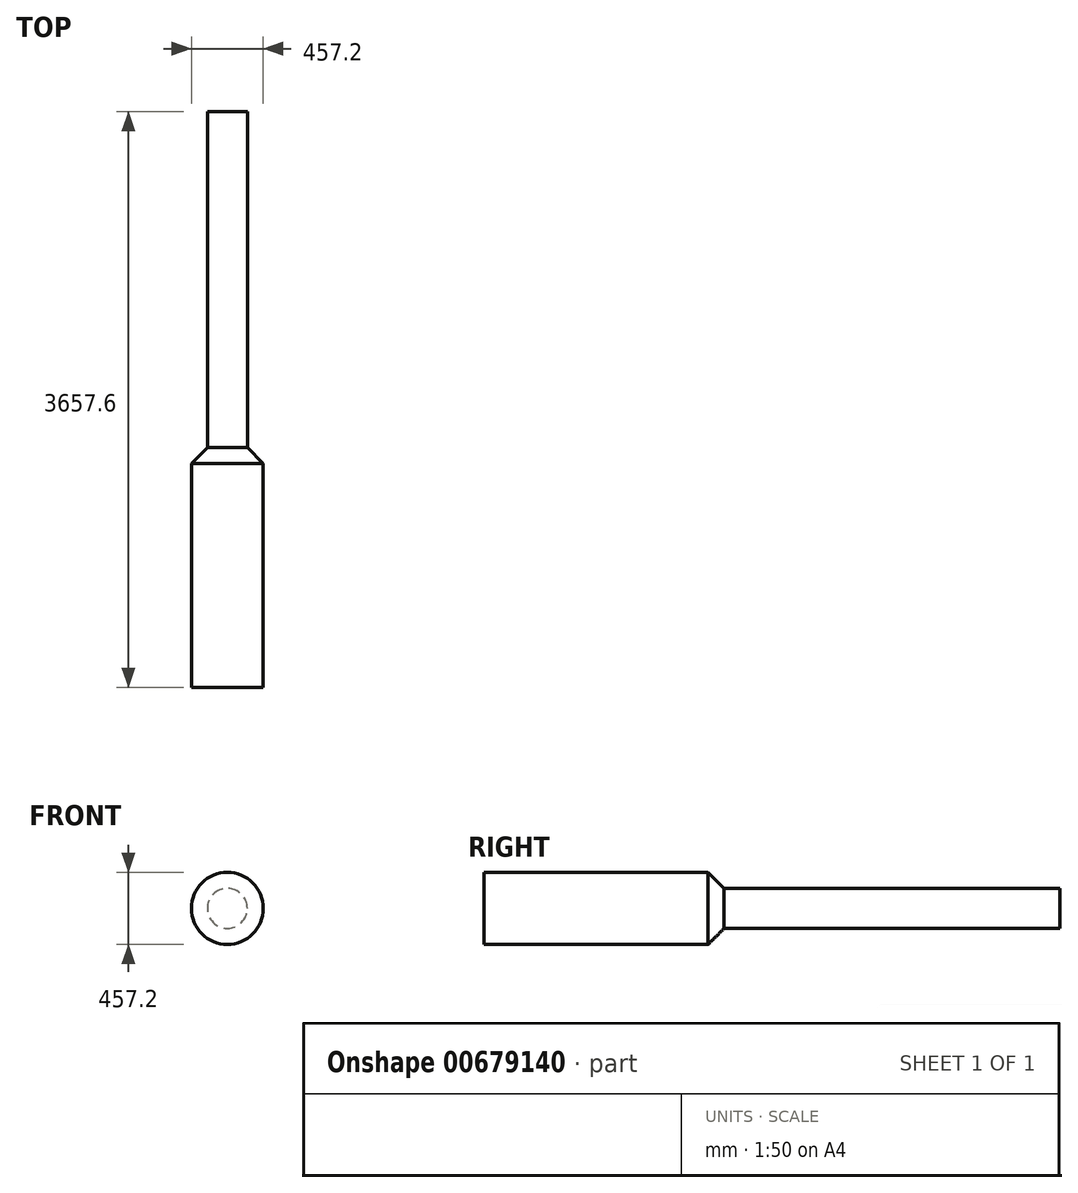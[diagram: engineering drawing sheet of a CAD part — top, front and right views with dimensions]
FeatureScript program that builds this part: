
annotation { "Feature Type Name" : "Feature", "Feature Type Description" : "" }
export const myFeature = defineFeature(function(context is Context, id is Id, definition is map)
    precondition{}
    {
        {
            var Q0;
            Q0=qCreatedBy(makeId("Right.planeOp"),FACE);
            var sketch = newSketch(context, id + "F0", { "sketchPlane" : qUnion([Q0])});
            skLineSegment(sketch, "E0.top", {"start": v(0, 228.6) * mm, "end": v(1422.4, 228.6) * mm});
            skLineSegment(sketch, "E0.left", {"start": v(0, 0) * mm, "end": v(0, 228.6) * mm});
            skLineSegment(sketch, "E1.top", {"start": v(1524, 127) * mm, "end": v(3657.6, 127) * mm});
            skLineSegment(sketch, "E1.right", {"start": v(3657.6, 0) * mm, "end": v(3657.6, 127) * mm});
            skLineSegment(sketch, "E2", {"start": v(1422.4, 228.6) * mm, "end": v(1524, 127) * mm});
            skPoint(sketch, "E1.bottom.start.orphan", {"position": v(723.9, 0) * mm});
            skLineSegment(sketch, "E3", {"start": v(0, 0) * mm, "end": v(3657.6, 0) * mm});
            skSolve(sketch);
        }
        {
            var Q0;
            Q0=makeQuery(id+"F0.imprint","IMPRINT",FACE,{"disambiguationData":[TD([[makeQuery(id+"F0.imprint","IMPRINT",EDGE,{"derivedFrom":sQuery(id+"F0.wireOp",EDGE,"E0.top")}),-1.0]])]});
            var Q1;
            Q1=sQuery(id+"F0.wireOp",EDGE,"E3");
            revolve(context, id + "F1", {"entities" : qUnion([Q0]), "axis" : qUnion([Q1]), "revolveType" : RevolveType.FULL});
        }
    });
